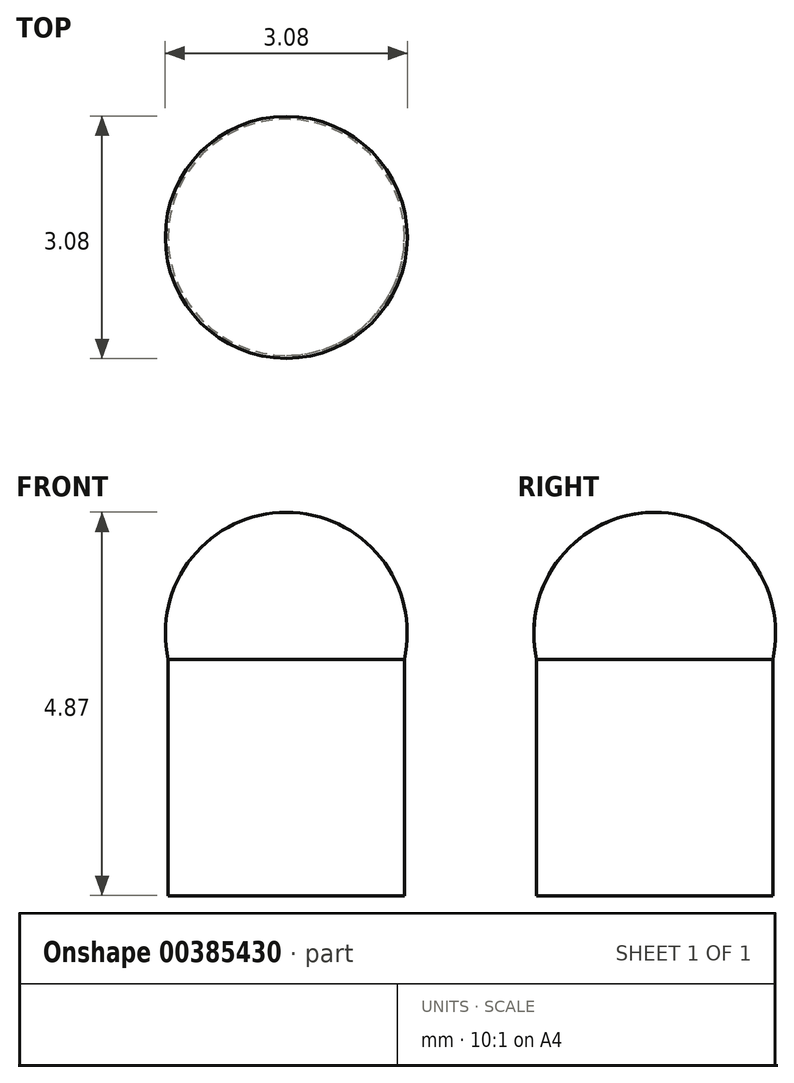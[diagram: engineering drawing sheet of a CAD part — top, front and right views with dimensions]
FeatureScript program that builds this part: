
annotation { "Feature Type Name" : "Feature", "Feature Type Description" : "" }
export const myFeature = defineFeature(function(context is Context, id is Id, definition is map)
    precondition{}
    {
        {
            var Q0;
            Q0=qCreatedBy(makeId("Right.planeOp"),FACE);
            var sketch = newSketch(context, id + "F0", { "sketchPlane" : qUnion([Q0])});
            skArc(sketch, "E0", {"start": v(0, 1.54) * mm, "mid": v(-1.2, 0.96) * mm, "end": v(-1.5, -0.33) * mm});
            skLineSegment(sketch, "E1", {"start": v(-1.5, -0.33) * mm, "end": v(-1.5, -3.33) * mm});
            skLineSegment(sketch, "E2", {"start": v(-1.5, -3.33) * mm, "end": v(0, -3.33) * mm});
            skLineSegment(sketch, "E3", {"start": v(0, 1.54) * mm, "end": v(0, -3.33) * mm});
            skSolve(sketch);
        }
        {
            var Q0;
            Q0=makeQuery(id+"F0.imprint","IMPRINT",FACE,{"disambiguationData":[TD([[makeQuery(id+"F0.imprint","IMPRINT",EDGE,{"derivedFrom":sQuery(id+"F0.wireOp",EDGE,"E0")}),1.0]])]});
            var Q1;
            Q1=sQuery(id+"F0.wireOp",EDGE,"E3");
            revolve(context, id + "F1", {"entities" : qUnion([Q0]), "axis" : qUnion([Q1]), "revolveType" : RevolveType.FULL});
        }
    });
